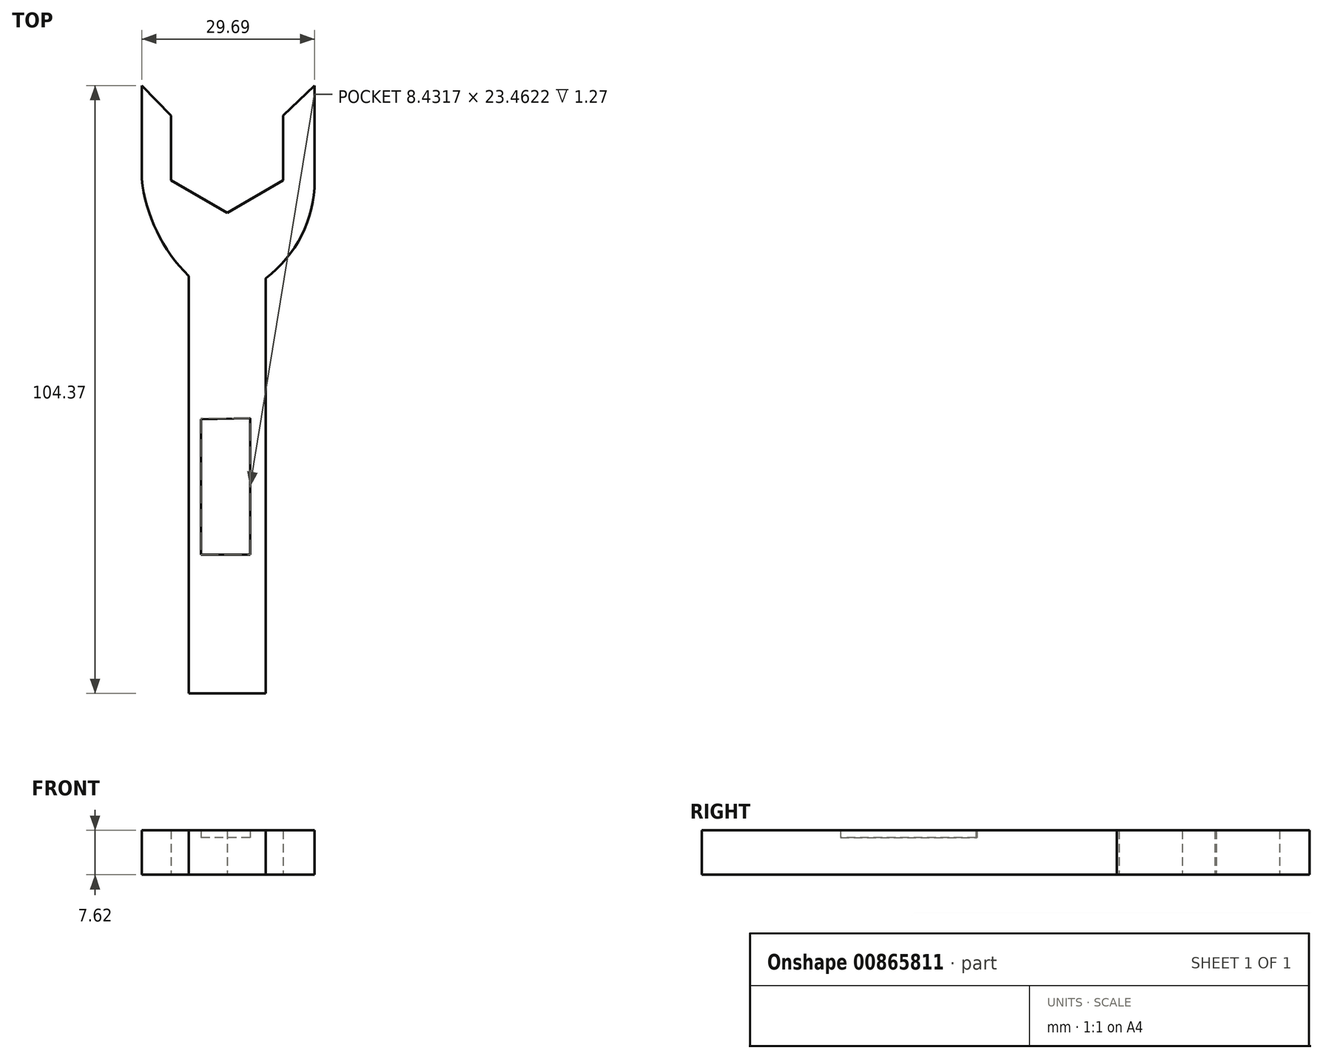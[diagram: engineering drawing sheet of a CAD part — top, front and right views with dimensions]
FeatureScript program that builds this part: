
annotation { "Feature Type Name" : "Feature", "Feature Type Description" : "" }
export const myFeature = defineFeature(function(context is Context, id is Id, definition is map)
    precondition{}
    {
        {
            var Q0;
            Q0=qCreatedBy(makeId("Top.planeOp"),FACE);
            var sketch = newSketch(context, id + "F0", { "sketchPlane" : qUnion([Q0])});
            skLineSegment(sketch, "E0.top", {"start": v(-39.4, -54.8) * mm, "end": v(-26.21, -54.8) * mm});
            skLineSegment(sketch, "E0.left", {"start": v(-39.4, 31.84) * mm, "end": v(-39.4, 31.54) * mm});
            skLineSegment(sketch, "E0.right", {"start": v(-26.21, 31.84) * mm, "end": v(-26.21, 31.54) * mm});
            skArc(sketch, "E1.cCircle", {"start": v(-40.67, 33.3) * mm, "mid": v(-39.3, 31.74) * mm, "end": v(-37.62, 30.51) * mm, "construction": true});
            skLineSegment(sketch, "E1.0", {"start": v(-23.19, 44.4) * mm, "end": v(-23.19, 33.3) * mm});
            skLineSegment(sketch, "E1.1", {"start": v(-23.19, 33.3) * mm, "end": v(-32.81, 27.73) * mm});
            skLineSegment(sketch, "E1.2", {"start": v(-32.81, 27.73) * mm, "end": v(-42.43, 33.3) * mm});
            skLineSegment(sketch, "E1.3", {"start": v(-42.43, 33.3) * mm, "end": v(-42.43, 44.4) * mm});
            skPoint(sketch, "E1.0.midPoint", {"position": v(-23.19, 38.85) * mm});
            skArc(sketch, "E2.trimOffspring", {"start": v(-28, 30.51) * mm, "mid": v(-27.07, 31.13) * mm, "end": v(-26.21, 31.84) * mm, "construction": true});
            skLineSegment(sketch, "E3.trimOffspring", {"start": v(-26.21, 16.5) * mm, "end": v(-26.21, -54.8) * mm});
            skLineSegment(sketch, "E4.trimOffspring", {"start": v(-39.4, 16.86) * mm, "end": v(-39.4, -54.8) * mm});
            skLineSegment(sketch, "E5", {"start": v(-47.47, 33.54) * mm, "end": v(-47.47, 49.58) * mm});
            skLineSegment(sketch, "E6", {"start": v(-47.47, 49.58) * mm, "end": v(-42.43, 44.4) * mm});
            skPoint(sketch, "E7.start.orphan", {"position": v(-19.25, 49.58) * mm});
            skLineSegment(sketch, "E8", {"start": v(-17.78, 49.58) * mm, "end": v(-23.19, 44.4) * mm});
            skArc(sketch, "E9", {"start": v(-47.47, 33.54) * mm, "mid": v(-44.87, 24.51) * mm, "end": v(-39.4, 16.86) * mm});
            skLineSegment(sketch, "E10", {"start": v(-17.78, 49.58) * mm, "end": v(-17.78, 33.18) * mm});
            skArc(sketch, "E11", {"start": v(-26.21, 16.5) * mm, "mid": v(-20, 23.83) * mm, "end": v(-17.78, 33.18) * mm});
            skLineSegment(sketch, "E12", {"start": v(-39.4, 16.86) * mm, "end": v(-26.21, 16.5) * mm});
            skLineSegment(sketch, "E13", {"start": v(-37.3, -7.7) * mm, "end": v(-37.3, -30.98) * mm});
            skLineSegment(sketch, "E14", {"start": v(-37.3, -30.98) * mm, "end": v(-28.87, -30.98) * mm});
            skLineSegment(sketch, "E15", {"start": v(-28.87, -30.98) * mm, "end": v(-28.87, -7.52) * mm});
            skLineSegment(sketch, "E16", {"start": v(-28.87, -7.52) * mm, "end": v(-37.3, -7.7) * mm});
            skSolve(sketch);
        }
        {
            var Q0;
            Q0 = qSketchRegion(id + "F0", true);
            extrude(context, id + "F1", {"entities" : qUnion([Q0]), "depth" : 7.62 * mm, "offsetDistance" : 25.4 * mm});
        }
        {
            var Q0;
            Q0=makeQuery(id+"F0.imprint","IMPRINT",FACE,{"disambiguationData":[TD([[makeQuery(id+"F0.imprint","IMPRINT",EDGE,{"derivedFrom":sQuery(id+"F0.wireOp",EDGE,"E13")}),1.0]])]});
            extrude(context, id + "F2", {"entities" : qUnion([Q0]), "operationType" : NewBodyOperationType.ADD, "depth" : 6.35 * mm, "offsetDistance" : 25.4 * mm});
        }
    });
